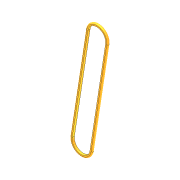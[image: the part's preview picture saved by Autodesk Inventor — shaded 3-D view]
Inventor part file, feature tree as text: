
AUTODESK INVENTOR PART (.ipt)
format: ipt  version: 2012 (Build 160160000, 160)  size: 96,768 bytes
history: native  units: in
note: dims shown in document units (in); Inventor stores cm internally (conversion verified against a paired STEP export)
features: extrude x1, fillet x1, sketch x1
ambient origin geometry x8: Origin, YZ Plane, XZ Plane, XY Plane, X Axis, Y Axis, Z Axis, Center Point
bodies: Solid1 (feature_tree)
feature tree (3):
  extrude  "Extrusion1"  Depth=0.1875in
  fillet  "Fillet1"  Radius=0.75in
  sketch  "Sketch1"  dims[d0=8.5in d1=0.1875in d2=0.75in d3=0.1875in d4=0.0in d5=0.0938in]
